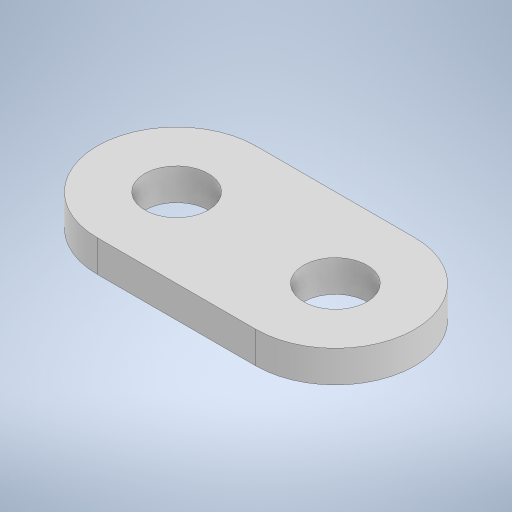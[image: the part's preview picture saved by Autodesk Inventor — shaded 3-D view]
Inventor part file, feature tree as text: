
AUTODESK INVENTOR PART (.ipt)
format: ipt  version: 2023 (Build 270158000, 158)  size: 223,744 bytes
history: native  units: mm
features: extrude x1, sketch x1
ambient origin geometry x8: Origin, YZ Plane, XZ Plane, XY Plane, X Axis, Y Axis, Z Axis, Center Point
bodies: Solid1 (feature_tree)
feature tree (2):
  extrude  "Extrusion1"  Depth=2.0mm
  sketch  "Sketch1"  dims[d0=10.0mm d1=4.0mm d3=20.0mm d4=2.0mm d5=0.0mm]
